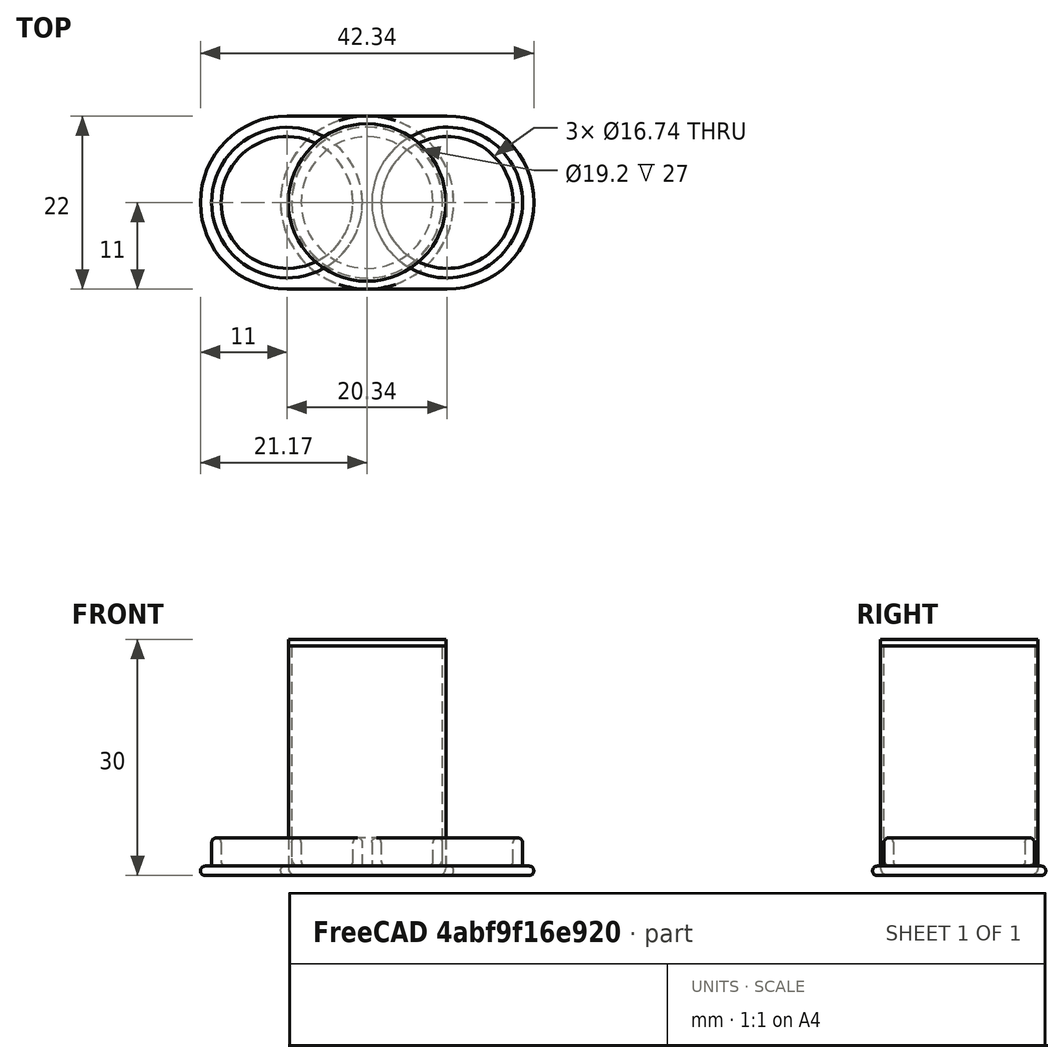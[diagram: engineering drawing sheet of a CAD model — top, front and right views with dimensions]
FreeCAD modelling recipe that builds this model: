
FCSTD DOCUMENT  (FreeCAD 0.18.3R)
Label: capsule
License: All rights reserved
LicenseURL: http://en.wikipedia.org/wiki/All_rights_reserved
objects: Sketcher::SketchObject×6, PartDesign::Pad×6, PartDesign::Fillet×4, PartDesign::Body×4, Mesh::Feature×2, App::Part×1, PartDesign::AdditiveCylinder×1
note: 28 computed .brp shape members not serialized (recipe doc carries the construction recipe); baked Part::Feature solids carry a one-line shape summary decoded from their .brp

FEATURE [Sketcher::SketchObject] Sketch
  MapMode = 5
  Support = -> [XY_Plane001]
  sketch-geometry (1):
    g0: Circle CenterX=0 CenterY=0 CenterZ=0 NormalX=0 NormalY=0 NormalZ=1 AngleXU=0 Radius=10
  constraints (2):
    c: Coincident(g0,g-1)
    c: Radius(g0) = 10  'Outer'
FEATURE [PartDesign::Pad] Pad
  Length = 1.2
  Length2 = 100
  Profile = -> Sketch
  Type = 0
FEATURE [Sketcher::SketchObject] Sketch001
  AttachmentOffset = pos=(0,0,1.2) rot=(0,0,1;0rad)
  MapMode = 5
  Placement = pos=(0,0,1.2) rot=(0,0,1;0rad)
  Support = -> [XY_Plane001]
  expr: Constraints.Outer = Sketch.Constraints.Outer
  expr: AttachmentOffset.Base.z = Sketch.AttachmentOffset.Base.z + Pad.Length
  sketch-geometry (3):
    g0: Circle CenterX=0 CenterY=0 CenterZ=0 NormalX=0 NormalY=0 NormalZ=1 AngleXU=0 Radius=10
    g1: Circle CenterX=0 CenterY=0 CenterZ=0 NormalX=0 NormalY=0 NormalZ=1 AngleXU=0 Radius=9.6
    g2: LineSegment [constr] StartX=9.6 StartY=0 StartZ=0 EndX=10 EndY=0 EndZ=0
  constraints (8):
    c: Coincident(g0,g-1)
    c: Radius(g0) = 10  'Outer'
    c: Coincident(g1,g0)
    c: PointOnObject(g2,g1)
    c: PointOnObject(g2,g0)
    c: Horizontal(g2)
    c: PointOnObject(g0,g2)
    c: DistanceX(g2,g2) = 0.4  'WallThickness'
FEATURE [PartDesign::Pad] Pad001
  BaseFeature = -> Pad
  Length = 28
  Length2 = 100
  Profile = -> Sketch001
  Refine = true
  Type = 0
FEATURE [PartDesign::Fillet] Fillet
  Base = -> Pad001 [Edge6,Edge1]
  BaseFeature = -> Pad001
  Radius = 1
FEATURE [PartDesign::Body] Body
  Group = -> [Sketch,Pad,Sketch001,Pad001,Fillet]
  Origin = -> Origin001
  Tip = -> Fillet
FEATURE [Sketcher::SketchObject] Sketch002
  MapMode = 5
  Support = -> [XY_Plane002]
  expr: Constraints.Inner = Sketch001.Constraints.Outer - Sketch001.Constraints.WallThickness - 0.03mm
  expr: Constraints[1] = Sketch.Constraints.Outer + 1mm
  sketch-geometry (2):
    g0: Circle CenterX=0 CenterY=0 CenterZ=0 NormalX=0 NormalY=0 NormalZ=1 AngleXU=0 Radius=11
    g1: Circle [constr] CenterX=0 CenterY=0 CenterZ=0 NormalX=0 NormalY=0 NormalZ=1 AngleXU=0 Radius=9.57
  constraints (4):
    c: Coincident(g0,g-1)
    c: Radius(g0) = 11
    c: Coincident(g1,g0)
    c: Radius(g1) = 9.57  'Inner'
FEATURE [PartDesign::Pad] Pad002
  Length = 1.2
  Length2 = 100
  Profile = -> Sketch002
  Type = 0
FEATURE [Sketcher::SketchObject] Sketch003
  AttachmentOffset = pos=(0,0,1.2) rot=(0,0,1;0rad)
  MapMode = 5
  Placement = pos=(0,0,1.2) rot=(0,0,1;0rad)
  Support = -> [XY_Plane002]
  expr: AttachmentOffset.Base.z = Pad002.Length
  expr: Constraints.Outer = Sketch002.Constraints.Inner
  expr: Constraints[1] = Constraints.Outer - 1.2mm
  sketch-geometry (2):
    g0: Circle CenterX=0 CenterY=0 CenterZ=0 NormalX=0 NormalY=0 NormalZ=1 AngleXU=0 Radius=8.37
    g1: Circle CenterX=0 CenterY=0 CenterZ=0 NormalX=0 NormalY=0 NormalZ=1 AngleXU=0 Radius=9.57
  constraints (4):
    c: Coincident(g0,g-1)
    c: Radius(g0) = 8.37
    c: Coincident(g1,g0)
    c: Radius(g1) = 9.57  'Outer'
FEATURE [PartDesign::Pad] Pad003
  BaseFeature = -> Pad002
  Length = 3.6
  Length2 = 100
  Profile = -> Sketch003
  Type = 0
FEATURE [PartDesign::Fillet] Fillet001
  Base = -> Pad003 [Edge2,Edge3,Edge9,Edge6,Edge7]
  BaseFeature = -> Pad003
  Radius = 0.59
FEATURE [PartDesign::Body] Body001
  Group = -> [Sketch002,Pad002,Sketch003,Pad003,Fillet001]
  Origin = -> Origin002
  Tip = -> Fillet001
FEATURE [App::Part] Part
  Group = -> [Body,Body001]
  Origin = -> Origin
FEATURE [Mesh::Feature] Mesh  label="Fillet (Meshed)"
FEATURE [Mesh::Feature] Mesh001  label="Fillet001 (Meshed)"
FEATURE [Sketcher::SketchObject] Sketch004
  MapMode = 5
  Support = -> [XY_Plane003]
  expr: Constraints.Outer = Sketch.Constraints.Outer + 1mm
  expr: Constraints.Inner = Sketch001.Constraints.Outer - Sketch001.Constraints.WallThickness - 0.03mm
  sketch-geometry (9):
    g0: Circle [constr] CenterX=-10.17 CenterY=0 CenterZ=0 NormalX=0 NormalY=0 NormalZ=1 AngleXU=0 Radius=9.57
    g1: Circle [constr] CenterX=10.17 CenterY=0 CenterZ=0 NormalX=0 NormalY=0 NormalZ=1 AngleXU=0 Radius=9.57
    g2: LineSegment [constr] StartX=-10.17 StartY=0 StartZ=0 EndX=-0.6 EndY=0 EndZ=0
    g3: LineSegment [constr] StartX=-0.6 StartY=0 StartZ=0 EndX=0.6 EndY=0 EndZ=0
    g4: LineSegment [constr] StartX=0.6 StartY=0 StartZ=0 EndX=10.17 EndY=0 EndZ=0
    g5: ArcOfCircle CenterX=-10.17 CenterY=0 CenterZ=0 NormalX=0 NormalY=0 NormalZ=1 AngleXU=0 Radius=11 StartAngle=1.5708 EndAngle=4.71239
    g6: ArcOfCircle CenterX=10.17 CenterY=0 CenterZ=0 NormalX=0 NormalY=0 NormalZ=1 AngleXU=0 Radius=11 StartAngle=4.71239 EndAngle=7.85398
    g7: LineSegment StartX=-10.17 StartY=-11 StartZ=0 EndX=10.17 EndY=-11 EndZ=0
    g8: LineSegment StartX=-10.17 StartY=11 StartZ=0 EndX=10.17 EndY=11 EndZ=0
  constraints (21):
    c: Radius(g0) = 9.57  'Inner'
    c: Equal(g0,g1)
    c: PointOnObject(g2,g0)
    c: Horizontal(g2)
    c: Coincident(g3,g2)
    c: PointOnObject(g3,g1)
    c: Horizontal(g3)
    c: Coincident(g4,g3)
    c: Coincident(g4,g1)
    c: Horizontal(g4)
    c: DistanceX(g3,g3) = 1.2
    c: Coincident(g5,g0)
    c: Coincident(g6,g1)
    c: Radius(g5) = 11  'Outer'
    c: Coincident(g0,g2)
    c: Equal(g5,g6)
    c: Tangent(g5,g8) = 1.5708
    c: Tangent(g5,g7) = -1.5708
    c: Tangent(g6,g7) = -1.5708
    c: Tangent(g6,g8) = 1.5708
    c: Symmetric(g2,g3,g-1)  '__ANCHOR__'
FEATURE [PartDesign::Pad] Pad004
  Length = 1.2
  Length2 = 100
  Profile = -> Sketch004
  Type = 0
FEATURE [Sketcher::SketchObject] Sketch005
  AttachmentOffset = pos=(0,0,1.2) rot=(0,0,1;0rad)
  MapMode = 5
  Placement = pos=(0,0,1.2) rot=(0,0,1;0rad)
  Support = -> [XY_Plane003]
  expr: Constraints[24] = Constraints.Outer - 1.2mm
  expr: AttachmentOffset.Base.z = Pad004.Length
  expr: Constraints[13] = Sketch004.Constraints.Outer
  expr: Constraints.Outer = Sketch004.Constraints.Inner
  sketch-geometry (11):
    g0: Circle CenterX=-10.17 CenterY=0 CenterZ=0 NormalX=0 NormalY=0 NormalZ=1 AngleXU=0 Radius=9.57
    g1: Circle CenterX=10.17 CenterY=0 CenterZ=0 NormalX=0 NormalY=0 NormalZ=1 AngleXU=0 Radius=9.57
    g2: LineSegment [constr] StartX=-10.17 StartY=0 StartZ=0 EndX=-0.6 EndY=0 EndZ=0
    g3: LineSegment [constr] StartX=-0.6 StartY=0 StartZ=0 EndX=0.6 EndY=0 EndZ=0
    g4: LineSegment [constr] StartX=0.6 StartY=0 StartZ=0 EndX=10.17 EndY=0 EndZ=0
    g5: ArcOfCircle [constr] CenterX=-10.17 CenterY=0 CenterZ=0 NormalX=0 NormalY=0 NormalZ=1 AngleXU=0 Radius=11 StartAngle=1.5708 EndAngle=4.71239
    g6: ArcOfCircle [constr] CenterX=10.17 CenterY=0 CenterZ=0 NormalX=0 NormalY=0 NormalZ=1 AngleXU=0 Radius=11 StartAngle=4.71239 EndAngle=7.85398
    g7: LineSegment [constr] StartX=-10.17 StartY=-11 StartZ=0 EndX=10.17 EndY=-11 EndZ=0
    g8: LineSegment [constr] StartX=-10.17 StartY=11 StartZ=0 EndX=10.17 EndY=11 EndZ=0
    g9: Circle CenterX=-10.17 CenterY=0 CenterZ=0 NormalX=0 NormalY=0 NormalZ=1 AngleXU=0 Radius=8.37
    g10: Circle CenterX=10.17 CenterY=0 CenterZ=0 NormalX=0 NormalY=0 NormalZ=1 AngleXU=0 Radius=8.37
  constraints (25):
    c: Radius(g0) = 9.57  'Outer'
    c: Equal(g0,g1)
    c: PointOnObject(g2,g0)
    c: Horizontal(g2)
    c: Coincident(g3,g2)
    c: PointOnObject(g3,g1)
    c: Horizontal(g3)
    c: Coincident(g4,g3)
    c: Coincident(g4,g1)
    c: Horizontal(g4)
    c: DistanceX(g3,g3) = 1.2
    c: Coincident(g5,g0)
    c: Coincident(g6,g1)
    c: Radius(g5) = 11
    c: Coincident(g0,g2)
    c: Equal(g5,g6)
    c: Tangent(g5,g8) = 1.5708
    c: Tangent(g5,g7) = -1.5708
    c: Tangent(g6,g7) = -1.5708
    c: Tangent(g6,g8) = 1.5708
    c: Symmetric(g2,g3,g-1)  '__ANCHOR__'
    c: Coincident(g9,g0)
    c: Coincident(g10,g1)
    c: Equal(g9,g10)
    c: Radius(g9) = 8.37
FEATURE [PartDesign::Pad] Pad005
  BaseFeature = -> Pad004
  Length = 3.6
  Length2 = 100
  Profile = -> Sketch005
  Type = 0
FEATURE [PartDesign::Fillet] Fillet002
  Base = -> Pad005 [Edge9,Edge10,Edge18,Edge16,Edge20,Edge19,Edge24,Edge22]
  BaseFeature = -> Pad005
  Radius = 0.599
FEATURE [PartDesign::Body] Body002
  Group = -> [Sketch004,Pad004,Sketch005,Pad005,Fillet002]
  Origin = -> Origin003
  Tip = -> Fillet002
FEATURE [PartDesign::AdditiveCylinder] Cylinder
  Angle = 360
  AttacherType = Attacher::AttachEngine3D
  Height = 30
  Radius = 10
FEATURE [PartDesign::Fillet] Fillet003
  Base = -> Cylinder [Edge3]
  BaseFeature = -> Cylinder
  Radius = 1
FEATURE [PartDesign::Body] Body003
  Group = -> [Cylinder,Fillet003]
  Origin = -> Origin004
  Tip = -> Fillet003
